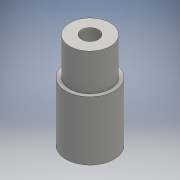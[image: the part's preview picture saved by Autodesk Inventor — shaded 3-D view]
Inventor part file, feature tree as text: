
AUTODESK INVENTOR PART (.ipt)
format: ipt  version: 2016 (Build 200138000, 138)  size: 100,864 bytes
history: native  units: mm
features: extrude x2, other x1, sketch x1
ambient origin geometry x8: Origin, YZ Plane, XZ Plane, XY Plane, X Axis, Y Axis, Z Axis, Center Point
bodies: Body1 (feature_tree)
feature tree (4):
  other  "ソリッド1"
  sketch  "スケッチ1"
  extrude  "押し出し1"  Depth=2.3mm
  extrude  "押し出し2"  Depth=6.5mm
